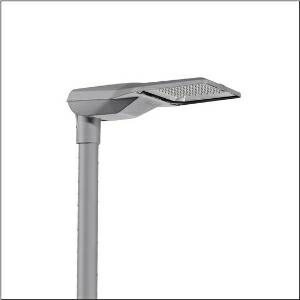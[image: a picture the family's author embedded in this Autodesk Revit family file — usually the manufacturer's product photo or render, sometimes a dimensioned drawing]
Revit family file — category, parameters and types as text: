
# Revit family: streetlight_sl_21_iq_midi___p0_8a_5xe3u31d08nb_0b79
name_source: partatom
category: Lighting Fixtures
units: mm (PartAtom-declared; Revit-internal decimal feet)

## family parameters
Cut with Voids When Loaded = No
Host = Face
Light Source = No
Part Type = Normal
Room Calculation Point = No
Round Connector Dimension = Use Diameter
Shared = No

## types (1)
- --- (1 x LED, 23430 lm, 155.5 W, 3000K)
    Apparent Load = 155 VA
    CIE Flux Codes = 36 69 97 100 100
    Color Rendering = 70
    Color Temperature = 3000K
    Default Elevation = 1800 mm
    Description = Streetlight SL 21 iQ midi, mast luminaire, primary light control with lens, of PMMA, primary optical cover: cover, of toughened safety glass, transparent, light distribution: P0.8a, light emission: direct distribution, primary light characteristic: asymmetric, installation type: post-top, side-entry, LED, High Power LED, rated luminous flux: 23.430lm, luminous efficacy: 151lm/W, light colour: 730, colour temperature: 3000K, control gear: iQ-Comfort, control: pre-setting: linear dimming characteristic, Auto-Match, Temp-Guard, Lumen-Switch, Night-Set, Smart-Wire, Light-Fading, Desk-Remote (wireless, voltage-free reading and setting of iQ features in the workshop via application-optimized NFC function/RFID function), optimised constant luminous flux control (CLO 2.0), mains connection: 230..240V, AC, 50/60Hz, start of lifetime: 156W, end of service life: 162W, reduction: 69W, luminaire housing, of diecast aluminium, powder-coated, Siteco® metallic grey (DB 702S), corrosivity category C5 mid according to DIN EN ISO 12944, please order mast flange separately, inclination adjustable: 0°, 5°, 10°, 15°, sealing non-destructively replaceable, multi-level sealing system, length: 644mm, width: 335mm, height: 110mm, mast flange for spigot size: 42mm (side-entry): 5XC10008XM4, 60/48mm (side-entry/post-top): 5XC10108XM2, 76/60mm (side-entry/post-top): 5XC10108XM1, mounting height: 4..8m, protection rating (complete): IP66, insulation class (complete): insulation class II (safety insulation), certification: CE, ENEC, ENEC+, VDE, impact resistance: IK10, permissible operating ambient temperature for outdoor applications: -40..+50°C, standard-compliant lighting for roads and squares, packaging unit: 1 piece

Light Distribution: P0.8a
    Height = 111 mm
    Lamp = 1 x LED
    Lamp Light Flux = 23430 lm
    Lamp Power = 155.5 W
    Lamp count = 1
    Length = 644 mm
    Luminous efficacy = 151 lm/W
    Manufacturer = Siteco
    ModVariant = No
    Model = 5XE3U31D08NB
    Number of Poles = 1
    OnlyDefault = Yes
    Power Factor = 1
    Product Name = Streetlight SL 21 iQ midi | P0.8a
    Product group = mast luminaire | pylon top
    ProductGroupID = 6100
    Protection Class = Protection class II
    Protection Degree = IP 66
    RLX_Detail_Level = 1
    RLX_Emergency_Light_Flux = 0 lm
    RLX_Emergency_Type = 0
    RLX_Emergency_Type_DB = No
    RlxData = <blob elided: 26965 chars, md5=4bb05644>
    Socket = socket
    Standby Power = 0 W
    System Light Flux = 23431 lm
    System Power = 155 W
    Type Comments = factory setting: luminous flux: 100 % | dim-lin: 254 | 823 mA
    Type Image = l_1004298.jpg
    URL = http://relux.com
    VarID = @adj_071556
    Voltage = 0 V
    Weight = 0.00 kg
    Width = 336 mm

## geometry (parser evidence)
native form markers: Blend x4, Sweep x12
no freeform markers — native parametric forms only
